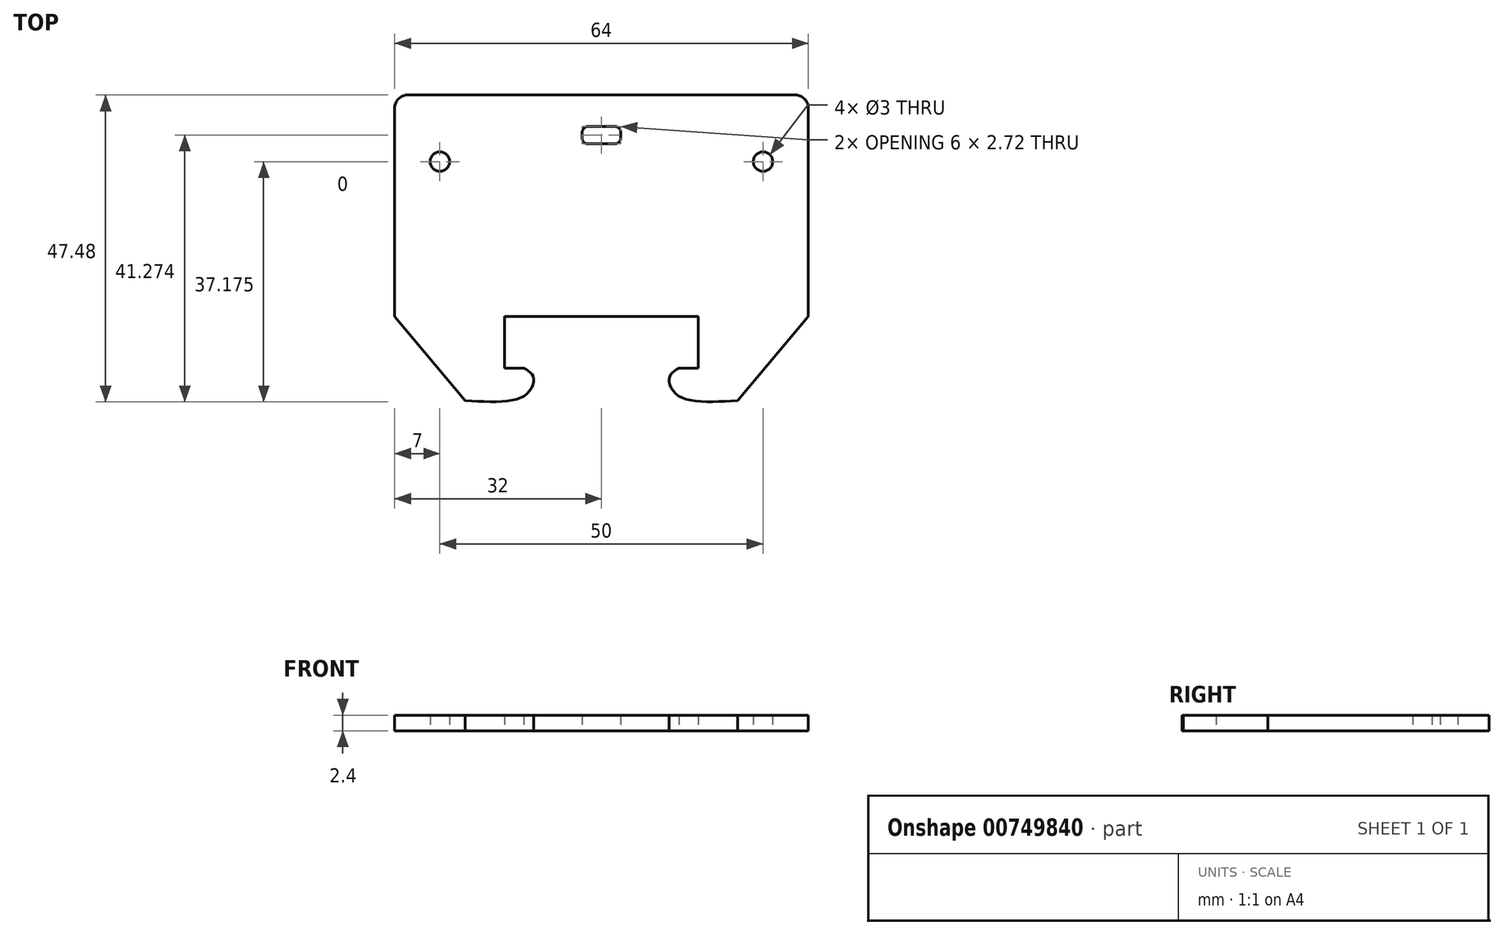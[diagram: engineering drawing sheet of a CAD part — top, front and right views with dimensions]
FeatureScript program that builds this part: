
annotation { "Feature Type Name" : "Feature", "Feature Type Description" : "" }
export const myFeature = defineFeature(function(context is Context, id is Id, definition is map)
    precondition{}
    {
        {
            var Q0;
            Q0=qCreatedBy(makeId("Top.planeOp"),FACE);
            var sketch = newSketch(context, id + "F0", { "sketchPlane" : qUnion([Q0])});
            skLineSegment(sketch, "E0.bottom", {"start": v(-30, 15.12) * mm, "end": v(30, 15.12) * mm});
            skLineSegment(sketch, "E0.top", {"start": v(-32, -15.12) * mm, "end": v(32, -15.12) * mm});
            skLineSegment(sketch, "E0.left", {"start": v(-32, 13.12) * mm, "end": v(-32, -15.12) * mm});
            skLineSegment(sketch, "E0.right", {"start": v(32, 13.12) * mm, "end": v(32, -15.12) * mm});
            skPoint(sketch, "E0.middle", {"position": v(0, 0) * mm});
            skLineSegment(sketch, "E1", {"start": v(-32, -15.12) * mm, "end": v(-32, -19.12) * mm});
            skLineSegment(sketch, "E2", {"start": v(-32, -19.12) * mm, "end": v(32, -19.13) * mm});
            skLineSegment(sketch, "E3", {"start": v(32, -19.12) * mm, "end": v(32, -15.12) * mm});
            skLineSegment(sketch, "E4", {"start": v(0, 0) * mm, "end": v(0, -19.12) * mm, "construction": true});
            skLineSegment(sketch, "E5", {"start": v(0, -19.12) * mm, "end": v(-15, -19.12) * mm});
            skLineSegment(sketch, "E6", {"start": v(-15, -19.12) * mm, "end": v(0, -19.12) * mm});
            skLineSegment(sketch, "E7", {"start": v(-15, -19.12) * mm, "end": v(-15, -27.13) * mm});
            skLineSegment(sketch, "E8", {"start": v(15, -19.12) * mm, "end": v(15, -27.13) * mm});
            skLineSegment(sketch, "E9", {"start": v(-15, -27.13) * mm, "end": v(-12, -27.13) * mm});
            skLineSegment(sketch, "E10", {"start": v(15, -27.13) * mm, "end": v(12, -27.13) * mm});
            skLineSegment(sketch, "E11", {"start": v(-32, -19.13) * mm, "end": v(-21.07, -32.15) * mm});
            skFitSpline(sketch, "E12", {"points": [v(-21.07, -32.15) * mm, v(-11.82, -31.35) * mm, v(-10.54, -28.54) * mm, v(-12, -27.12) * mm], "startDerivative": vector(22.71, -1.51) * mm, "endDerivative": vector(-8.34, 4.91) * mm});
            skFitSpline(sketch, "E13.MirrorCS", {"points": [v(21.07, -32.15) * mm, v(11.82, -31.35) * mm, v(10.54, -28.54) * mm, v(12, -27.12) * mm], "startDerivative": vector(-22.71, -1.51) * mm, "endDerivative": vector(8.34, 4.91) * mm});
            skLineSegment(sketch, "E14", {"start": v(21.07, -32.15) * mm, "end": v(32, -19.13) * mm});
            skLineSegment(sketch, "E15", {"start": v(0, 0) * mm, "end": v(0, 15.12) * mm});
            skLineSegment(sketch, "E16", {"start": v(0, 15.12) * mm, "end": v(0, 10.28) * mm});
            skLineSegment(sketch, "E17", {"start": v(0, 10.28) * mm, "end": v(0, 7.56) * mm});
            skLineSegment(sketch, "E18.bottom", {"start": v(-2, 10.28) * mm, "end": v(2, 10.28) * mm});
            skLineSegment(sketch, "E18.top", {"start": v(-2.1, 7.56) * mm, "end": v(2, 7.56) * mm});
            skLineSegment(sketch, "E18.left", {"start": v(-3, 9.28) * mm, "end": v(-3, 8.46) * mm});
            skLineSegment(sketch, "E18.right", {"start": v(3, 9.28) * mm, "end": v(3, 8.56) * mm});
            skPoint(sketch, "E18.middle", {"position": v(0, 8.92) * mm});
            skPoint(sketch, "E19.visualSharp", {"position": v(-3, 10.28) * mm});
            skArc(sketch, "E19.filletArc", {"start": v(-2, 10.28) * mm, "mid": v(-2.7, 10) * mm, "end": v(-3, 9.28) * mm});
            skPoint(sketch, "E20.visualSharp", {"position": v(3, 10.28) * mm});
            skArc(sketch, "E20.filletArc", {"start": v(3, 9.28) * mm, "mid": v(2.7, 10) * mm, "end": v(2, 10.28) * mm});
            skPoint(sketch, "E21.visualSharp", {"position": v(3, 7.56) * mm});
            skArc(sketch, "E21.filletArc", {"start": v(2, 7.56) * mm, "mid": v(2.7, 7.86) * mm, "end": v(3, 8.56) * mm});
            skPoint(sketch, "E22.visualSharp", {"position": v(-3, 7.56) * mm});
            skArc(sketch, "E22.filletArc", {"start": v(-3, 8.46) * mm, "mid": v(-2.74, 7.83) * mm, "end": v(-2.1, 7.56) * mm});
            skLineSegment(sketch, "E23", {"start": v(-25, 15.12) * mm, "end": v(-25, 4.82) * mm, "construction": true});
            skLineSegment(sketch, "E24", {"start": v(-25, 4.82) * mm, "end": v(-32, 4.82) * mm, "construction": true});
            skCircle(sketch, "E25", {"center": v(-25, 4.82) * mm, "radius": 1.5 * mm});
            skCircle(sketch, "E26.MirrorC", {"center": v(25, 4.82) * mm, "radius": 1.5 * mm});
            skPoint(sketch, "E27.visualSharp", {"position": v(-32, 15.12) * mm});
            skArc(sketch, "E27.filletArc", {"start": v(-30, 15.12) * mm, "mid": v(-31.41, 14.54) * mm, "end": v(-32, 13.12) * mm});
            skPoint(sketch, "E28.visualSharp", {"position": v(32, 15.12) * mm});
            skArc(sketch, "E28.filletArc", {"start": v(32, 13.12) * mm, "mid": v(31.41, 14.54) * mm, "end": v(30, 15.12) * mm});
            skSolve(sketch);
        }
        {
            var Q0;
            Q0 = qSketchRegion(id + "F0", true);
            extrude(context, id + "F1", {"entities" : qUnion([Q0]), "depth" : 2.4 * mm, "offsetDistance" : 25 * mm});
        }
    });
